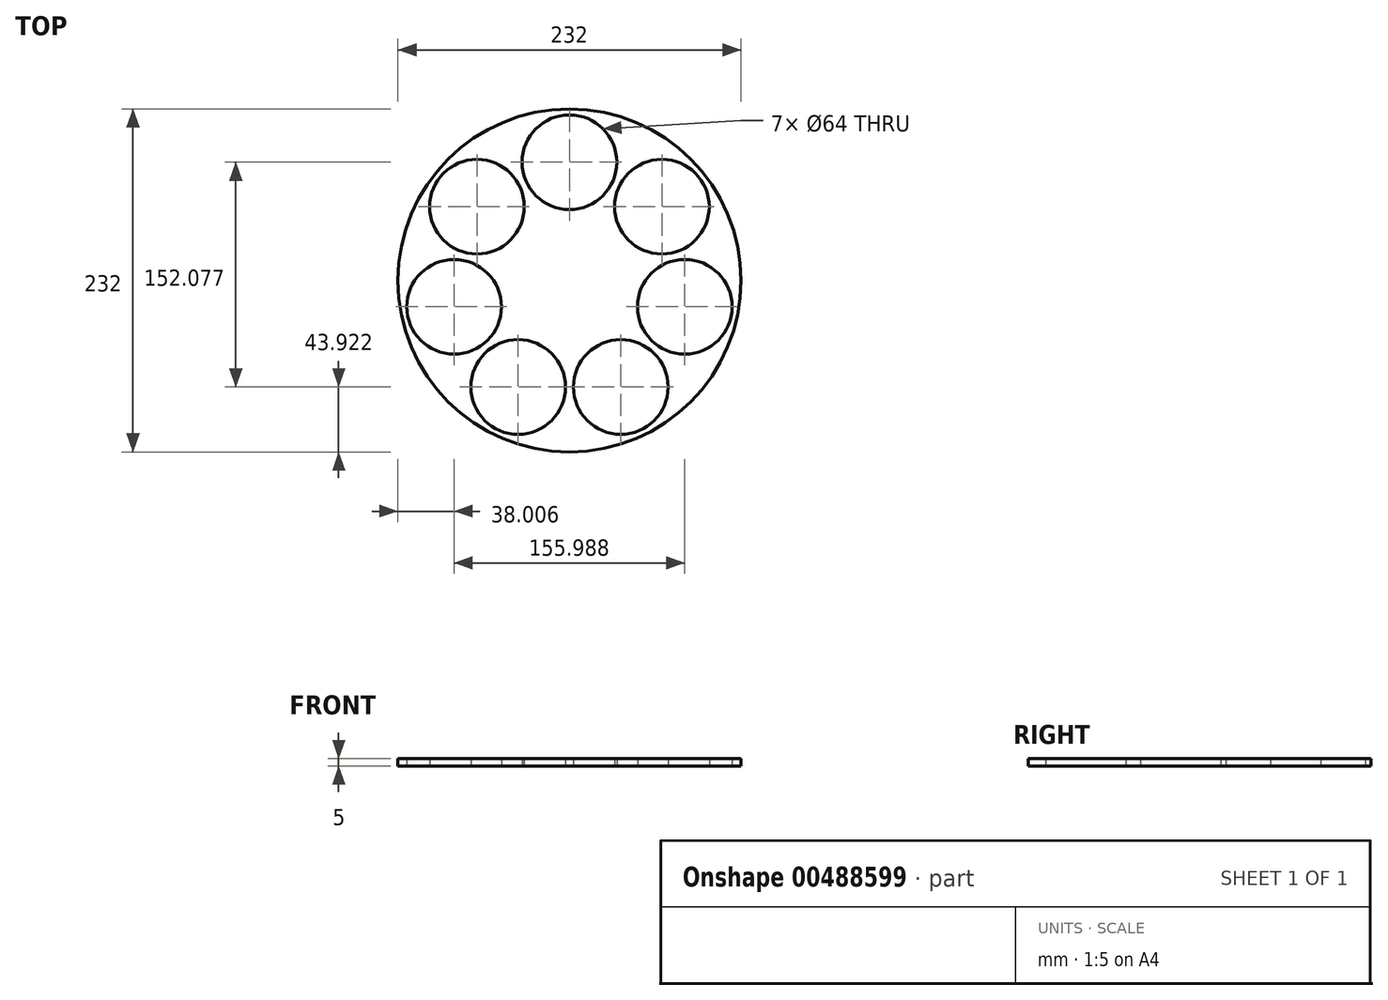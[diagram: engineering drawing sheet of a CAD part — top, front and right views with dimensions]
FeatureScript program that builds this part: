
annotation { "Feature Type Name" : "Feature", "Feature Type Description" : "" }
export const myFeature = defineFeature(function(context is Context, id is Id, definition is map)
    precondition{}
    {
        {
            var Q0;
            Q0=qCreatedBy(makeId("Top.planeOp"),FACE);
            var sketch = newSketch(context, id + "F0", { "sketchPlane" : qUnion([Q0])});
            skLineSegment(sketch, "E0", {"start": v(0, 0) * mm, "end": v(0, 80) * mm, "construction": true});
            skCircle(sketch, "E1", {"center": v(0, 80) * mm, "radius": 31 * mm});
            skCircle(sketch, "E2", {"center": v(0, 80) * mm, "radius": 32 * mm});
            skCircle(sketch, "E3", {"center": v(0, 0) * mm, "radius": 80 * mm, "construction": true});
            skCircle(sketch, "E4.1.0", {"center": v(-62.55, 49.88) * mm, "radius": 31 * mm});
            skCircle(sketch, "E4.2.0", {"center": v(-78, -17.8) * mm, "radius": 31 * mm});
            skCircle(sketch, "E4.3.0", {"center": v(-34.71, -72.08) * mm, "radius": 31 * mm});
            skCircle(sketch, "E4.4.0", {"center": v(34.71, -72.08) * mm, "radius": 31 * mm});
            skCircle(sketch, "E4.5.0", {"center": v(78, -17.8) * mm, "radius": 31 * mm});
            skCircle(sketch, "E4.6.0", {"center": v(62.55, 49.88) * mm, "radius": 31 * mm});
            skCircle(sketch, "E5.1.1", {"center": v(-62.55, 49.88) * mm, "radius": 32 * mm});
            skCircle(sketch, "E5.2.1", {"center": v(-78, -17.8) * mm, "radius": 32 * mm});
            skCircle(sketch, "E5.3.1", {"center": v(-34.71, -72.08) * mm, "radius": 32 * mm});
            skCircle(sketch, "E5.4.1", {"center": v(34.71, -72.08) * mm, "radius": 32 * mm});
            skCircle(sketch, "E5.5.1", {"center": v(78, -17.8) * mm, "radius": 32 * mm});
            skCircle(sketch, "E5.6.1", {"center": v(62.55, 49.88) * mm, "radius": 32 * mm});
            skCircle(sketch, "E6", {"center": v(0, 0) * mm, "radius": 116 * mm});
            skSolve(sketch);
        }
        {
            var Q0;
            Q0=sQuery(id+"F0.wireOp",EDGE,"E2");
            var Q1;
            Q1=sQuery(id+"F0.wireOp",EDGE,"E1");
            extrude(context, id + "F1", {"bodyType" : ToolBodyType.SURFACE, "surfaceEntities" : qUnion([Q0, Q1]), "depth" : 3 * mm});
        }
        {
            var Q0;
            Q0 = qSketchRegion(id + "F0", true);
            extrude(context, id + "F2", {"entities" : qUnion([Q0]), "depth" : 5 * mm});
        }
    });
